# Revit family: 95800 041
name_source: partatom
category: Equipamento mecânico
units: mm (PartAtom-declared; Revit-internal decimal feet)

## family parameters
Compartilhado = Não
Corte com vazios quando carregada = Não
Cota do conector redondo = Utilizar diâmetro
Hospedeiro = Forro
Número OmniClass = 23.75.00.00
Ponto de cálculo do ambiente = Não
Sempre na vertical = Sim
Tipo de parte = Normal
Título OmniClass = Climate Control (HVAC)

## types (2) — shared parameters
Altura Total (Min. 1,025m / Máx. 1,250m) = 1.25 m
Classe da Construção = CLASSE I
Comando = Eletrônico
Código da Peça = 95800/041
Descrição = Coifa de Ilha com comando por voz
Disjuntor Termomagnético = 10 A
Fabricante = Tramontina
Filtro de carvão = 1 Filtro de carvão Ambifresh 5 Square
Filtro metálico = 1 Filtro metálico
Frequência = -10 Hz
Grau de Proteção = IPX0
Iluminação = Lâmpadas Leds [4 x 1,3 W - 12 V]
Informações Complementares = Outras opções de corres
Kit de Instalação = Acabamento do teto, suporte de fixação no teto, suporte de fixação no gesso
Material = Aço Inox escovado com acabamento Scotch Brite
Modelo = 95800/041
Modo Conectado = controle via aplicativo ou comandos de voz via Amazon Alexa
Modo de Instalação = Ilha
Nível de Ruído = 64 db(A) - cfe. Norma EN 60704
Peso Líquido (Kg) = 19.3
Potência Elétrica = 223 W
Segmento = Residencial
Tensão = 220 V
Vazão Máxima = 480 m3/h - cfe. Norma IEC 61591
Velocidades = 4 velocidades com timer
zero-valued in all types: Elevação padrão

## per-type parameters (varying)
| type | Linha | Produto | URL |
| 110 Volts | Prime | Coifa Cube Isla 40 Silent | https://global.tramontina.com |
| 220 Volts | Tube | COIFA DE ILHA TUBE ISLA 35 | http://www.tramontina.com.br |
